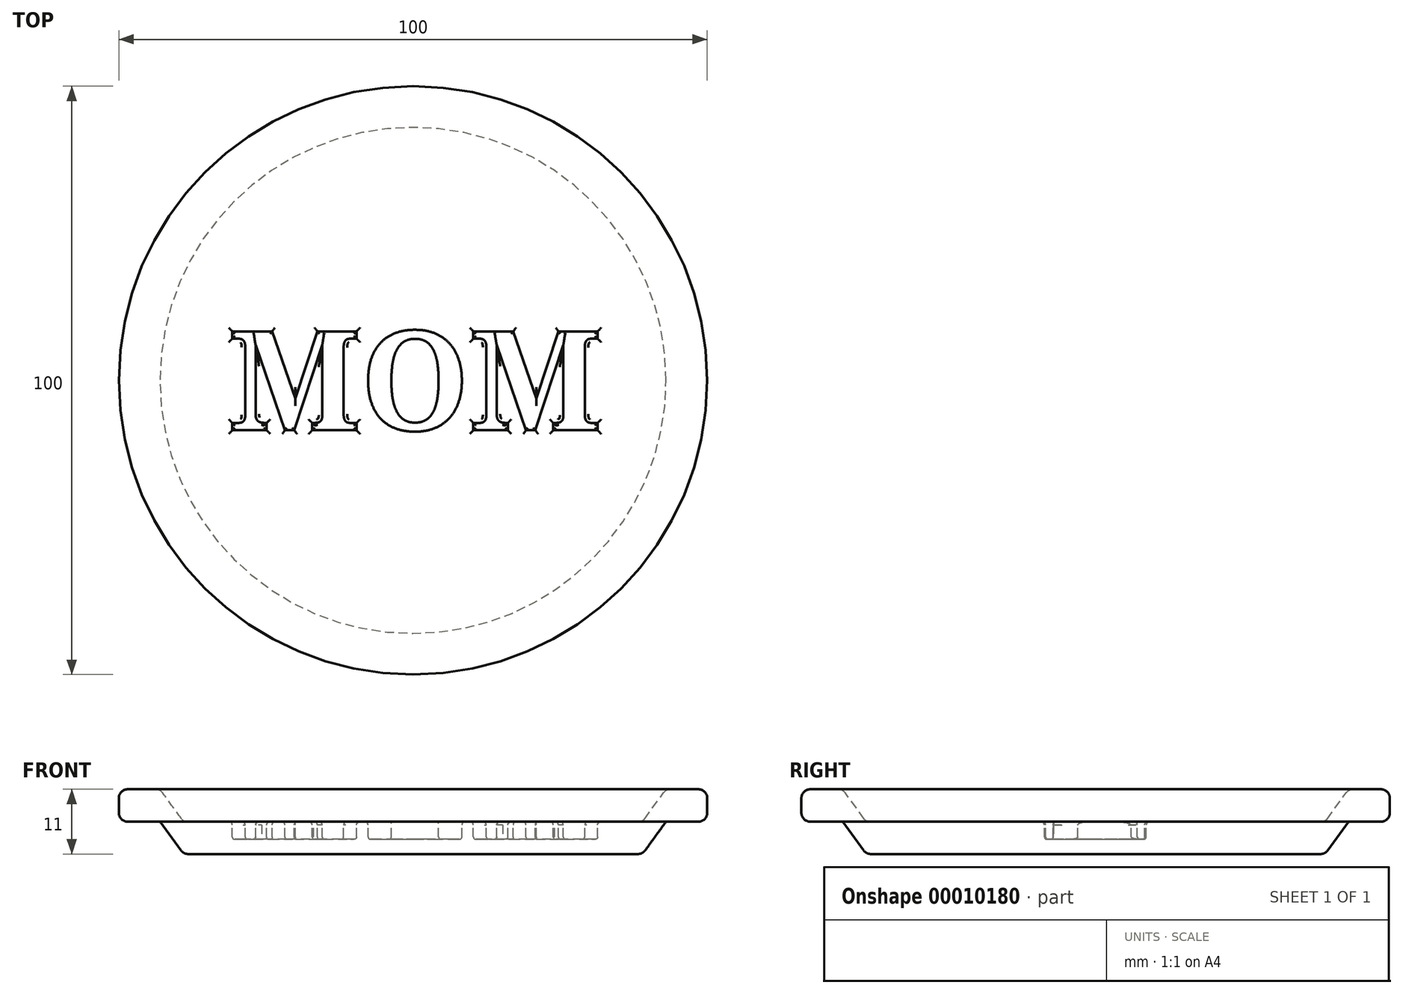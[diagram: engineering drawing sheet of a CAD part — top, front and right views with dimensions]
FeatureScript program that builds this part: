
annotation { "Feature Type Name" : "Feature", "Feature Type Description" : "" }
export const myFeature = defineFeature(function(context is Context, id is Id, definition is map)
    precondition{}
    {
        {
            var Q0;
            Q0=qCreatedBy(makeId("Front.planeOp"),FACE);
            var sketch = newSketch(context, id + "F0", { "sketchPlane" : qUnion([Q0])});
            skLineSegment(sketch, "E0", {"start": v(-39, 0) * mm, "end": v(0, 0) * mm});
            skLineSegment(sketch, "E1", {"start": v(-39, 0) * mm, "end": v(-43, 5.5) * mm});
            skLineSegment(sketch, "E2", {"start": v(-43, 5.5) * mm, "end": v(-50, 5.5) * mm});
            skLineSegment(sketch, "E3", {"start": v(-43, 0) * mm, "end": v(-39, 0) * mm, "construction": true});
            skLineSegment(sketch, "E4", {"start": v(-43, 0) * mm, "end": v(-43, 5.5) * mm, "construction": true});
            skLineSegment(sketch, "E5.0", {"start": v(-39, -5.5) * mm, "end": v(0, -5.5) * mm});
            skLineSegment(sketch, "E6.0", {"start": v(-43, 0) * mm, "end": v(-50, 0) * mm});
            skLineSegment(sketch, "E7", {"start": v(-43, 0) * mm, "end": v(-39, -5.5) * mm});
            skLineSegment(sketch, "E8", {"start": v(-50, 5.5) * mm, "end": v(-50, 0) * mm});
            skLineSegment(sketch, "E9", {"start": v(0, 0) * mm, "end": v(0, -5.5) * mm});
            skSolve(sketch);
        }
        {
            var Q0;
            Q0=qCreatedBy(makeId("Front.planeOp"),FACE);
            var sketch = newSketch(context, id + "F1", { "sketchPlane" : qUnion([Q0])});
            skLineSegment(sketch, "E10", {"start": v(0, 31.81) * mm, "end": v(0, -26.2) * mm});
            skSolve(sketch);
        }
        {
            var Q0;
            Q0=makeQuery(id+"F0.imprint","IMPRINT",FACE,{"disambiguationData":[TD([[makeQuery(id+"F0.imprint","IMPRINT",EDGE,{"derivedFrom":sQuery(id+"F0.wireOp",EDGE,"E0")}),-1.0]])]});
            var Q1;
            Q1=sQuery(id+"F1.wireOp",EDGE,"E10");
            revolve(context, id + "F2", {"entities" : qUnion([Q0]), "axis" : qUnion([Q1]), "revolveType" : RevolveType.FULL});
        }
        {
            var Q0;
            Q0=makeQuery(id+"F2.opRevolve","SWEPT_EDGE",EDGE,{"disambiguationData":[OSD([sQuery(id+"F0.wireOp",EDGE,"E1"),sQuery(id+"F0.wireOp",EDGE,"E2")])]});
            var Q1;
            Q1=makeQuery(id+"F2.opRevolve","SWEPT_EDGE",EDGE,{"disambiguationData":[OSD([sQuery(id+"F0.wireOp",EDGE,"E2"),sQuery(id+"F0.wireOp",EDGE,"E8")])]});
            var Q2;
            Q2=makeQuery(id+"F2.opRevolve","SWEPT_EDGE",EDGE,{"disambiguationData":[OSD([sQuery(id+"F0.wireOp",EDGE,"E6.0"),sQuery(id+"F0.wireOp",EDGE,"E8")])]});
            var Q3;
            Q3=makeQuery(id+"F2.opRevolve","SWEPT_EDGE",EDGE,{"disambiguationData":[OSD([sQuery(id+"F0.wireOp",EDGE,"E5.0"),sQuery(id+"F0.wireOp",EDGE,"E7")])]});
            fillet(context, id + "F3", {"entities" : qUnion([Q0, Q1, Q2, Q3]), "radius" : 1.5 * mm, "tangentPropagation" : true, "allowEdgeOverflow" : false});
        }
        {
            var Q0;
            Q0=makeQuery(id+"FGRXBjCafOSx1OX_1.boolean.opBoolean","COPY",EDGE,{"derivedFrom":makeQuery(id+"FGRXBjCafOSx1OX_1.opExtrude","CAP_EDGE",EDGE,{"disambiguationData":[OSD([sQuery(id+"FBqTZGQIcufDf44_1.wireOp",EDGE,"23bf69aa-c07b-4f37-bc8c-a48931fe9ff5.sketch_text.stroke-25")])],"isStart":true})});
            var Q1;
            Q1=makeQuery(id+"FGRXBjCafOSx1OX_1.boolean.opBoolean","COPY",EDGE,{"derivedFrom":makeQuery(id+"FGRXBjCafOSx1OX_1.opExtrude","CAP_EDGE",EDGE,{"disambiguationData":[OSD([sQuery(id+"FBqTZGQIcufDf44_1.wireOp",EDGE,"23bf69aa-c07b-4f37-bc8c-a48931fe9ff5.sketch_text.stroke-26")])],"isStart":true})});
            var Q2;
            Q2=makeQuery(id+"FGRXBjCafOSx1OX_1.boolean.opBoolean","SPLIT",FACE,{"disambiguationData":[TD([makeQuery(id+"F2.opRevolve","SWEPT_FACE",FACE,{"disambiguationData":[OSD([sQuery(id+"F0.wireOp",EDGE,"E1")])]})])],"derivedFrom":makeQuery(id+"F2.opRevolve","SWEPT_FACE",FACE,{"disambiguationData":[OSD([sQuery(id+"F0.wireOp",EDGE,"E0")])]})});
            var Q3;
            Q3=makeQuery(id+"FGRXBjCafOSx1OX_1.boolean.opBoolean","SPLIT",FACE,{"disambiguationData":[TD([makeQuery(id+"FGRXBjCafOSx1OX_1.opExtrude","SWEPT_FACE",FACE,{"disambiguationData":[OSD([sQuery(id+"FBqTZGQIcufDf44_1.wireOp",EDGE,"23bf69aa-c07b-4f37-bc8c-a48931fe9ff5.sketch_text.stroke-28")])]})])],"derivedFrom":makeQuery(id+"F2.opRevolve","SWEPT_FACE",FACE,{"disambiguationData":[OSD([sQuery(id+"F0.wireOp",EDGE,"E0")])]})});
            var Q4;
            Q4=makeQuery(id+"FGRXBjCafOSx1OX_1.boolean.opBoolean","SPLIT",FACE,{"disambiguationData":[TD([makeQuery(id+"FGRXBjCafOSx1OX_1.opExtrude","SWEPT_FACE",FACE,{"disambiguationData":[OSD([sQuery(id+"FBqTZGQIcufDf44_1.wireOp",EDGE,"23bf69aa-c07b-4f37-bc8c-a48931fe9ff5.sketch_text.stroke-39")])]})])],"derivedFrom":makeQuery(id+"F2.opRevolve","SWEPT_FACE",FACE,{"disambiguationData":[OSD([sQuery(id+"F0.wireOp",EDGE,"E0")])]})});
            var Q5;
            Q5=makeQuery(id+"FGRXBjCafOSx1OX_1.boolean.opBoolean","SPLIT",FACE,{"disambiguationData":[TD([makeQuery(id+"FGRXBjCafOSx1OX_1.opExtrude","SWEPT_FACE",FACE,{"disambiguationData":[OSD([sQuery(id+"FBqTZGQIcufDf44_1.wireOp",EDGE,"23bf69aa-c07b-4f37-bc8c-a48931fe9ff5.sketch_text.stroke-89")])]})])],"derivedFrom":makeQuery(id+"F2.opRevolve","SWEPT_FACE",FACE,{"disambiguationData":[OSD([sQuery(id+"F0.wireOp",EDGE,"E0")])]})});
            var Q6;
            Q6=makeQuery(id+"FGRXBjCafOSx1OX_1.boolean.opBoolean","SPLIT",FACE,{"disambiguationData":[TD([makeQuery(id+"FGRXBjCafOSx1OX_1.opExtrude","SWEPT_FACE",FACE,{"disambiguationData":[OSD([sQuery(id+"FBqTZGQIcufDf44_1.wireOp",EDGE,"23bf69aa-c07b-4f37-bc8c-a48931fe9ff5.sketch_text.stroke-78")])]})])],"derivedFrom":makeQuery(id+"F2.opRevolve","SWEPT_FACE",FACE,{"disambiguationData":[OSD([sQuery(id+"F0.wireOp",EDGE,"E0")])]})});
            var Q7;
            Q7=makeQuery(id+"FGRXBjCafOSx1OX_1.boolean.opBoolean","COPY",FACE,{"derivedFrom":makeQuery(id+"FGRXBjCafOSx1OX_1.opExtrude","CAP_FACE",FACE,{"disambiguationData":[OSD([sQuery(id+"FBqTZGQIcufDf44_1.wireOp",EDGE,"23bf69aa-c07b-4f37-bc8c-a48931fe9ff5.sketch_text.stroke-50"),sQuery(id+"FBqTZGQIcufDf44_1.wireOp",EDGE,"23bf69aa-c07b-4f37-bc8c-a48931fe9ff5.sketch_text.stroke-51"),sQuery(id+"FBqTZGQIcufDf44_1.wireOp",EDGE,"23bf69aa-c07b-4f37-bc8c-a48931fe9ff5.sketch_text.stroke-52"),sQuery(id+"FBqTZGQIcufDf44_1.wireOp",EDGE,"23bf69aa-c07b-4f37-bc8c-a48931fe9ff5.sketch_text.stroke-53"),sQuery(id+"FBqTZGQIcufDf44_1.wireOp",EDGE,"23bf69aa-c07b-4f37-bc8c-a48931fe9ff5.sketch_text.stroke-54"),sQuery(id+"FBqTZGQIcufDf44_1.wireOp",EDGE,"23bf69aa-c07b-4f37-bc8c-a48931fe9ff5.sketch_text.stroke-55"),sQuery(id+"FBqTZGQIcufDf44_1.wireOp",EDGE,"23bf69aa-c07b-4f37-bc8c-a48931fe9ff5.sketch_text.stroke-56"),sQuery(id+"FBqTZGQIcufDf44_1.wireOp",EDGE,"23bf69aa-c07b-4f37-bc8c-a48931fe9ff5.sketch_text.stroke-57"),sQuery(id+"FBqTZGQIcufDf44_1.wireOp",EDGE,"23bf69aa-c07b-4f37-bc8c-a48931fe9ff5.sketch_text.stroke-58"),sQuery(id+"FBqTZGQIcufDf44_1.wireOp",EDGE,"23bf69aa-c07b-4f37-bc8c-a48931fe9ff5.sketch_text.stroke-59"),sQuery(id+"FBqTZGQIcufDf44_1.wireOp",EDGE,"23bf69aa-c07b-4f37-bc8c-a48931fe9ff5.sketch_text.stroke-60"),sQuery(id+"FBqTZGQIcufDf44_1.wireOp",EDGE,"23bf69aa-c07b-4f37-bc8c-a48931fe9ff5.sketch_text.stroke-61"),sQuery(id+"FBqTZGQIcufDf44_1.wireOp",EDGE,"23bf69aa-c07b-4f37-bc8c-a48931fe9ff5.sketch_text.stroke-62"),sQuery(id+"FBqTZGQIcufDf44_1.wireOp",EDGE,"23bf69aa-c07b-4f37-bc8c-a48931fe9ff5.sketch_text.stroke-63"),sQuery(id+"FBqTZGQIcufDf44_1.wireOp",EDGE,"23bf69aa-c07b-4f37-bc8c-a48931fe9ff5.sketch_text.stroke-64"),sQuery(id+"FBqTZGQIcufDf44_1.wireOp",EDGE,"23bf69aa-c07b-4f37-bc8c-a48931fe9ff5.sketch_text.stroke-65"),sQuery(id+"FBqTZGQIcufDf44_1.wireOp",EDGE,"23bf69aa-c07b-4f37-bc8c-a48931fe9ff5.sketch_text.stroke-66"),sQuery(id+"FBqTZGQIcufDf44_1.wireOp",EDGE,"23bf69aa-c07b-4f37-bc8c-a48931fe9ff5.sketch_text.stroke-67"),sQuery(id+"FBqTZGQIcufDf44_1.wireOp",EDGE,"23bf69aa-c07b-4f37-bc8c-a48931fe9ff5.sketch_text.stroke-68"),sQuery(id+"FBqTZGQIcufDf44_1.wireOp",EDGE,"23bf69aa-c07b-4f37-bc8c-a48931fe9ff5.sketch_text.stroke-69"),sQuery(id+"FBqTZGQIcufDf44_1.wireOp",EDGE,"23bf69aa-c07b-4f37-bc8c-a48931fe9ff5.sketch_text.stroke-70"),sQuery(id+"FBqTZGQIcufDf44_1.wireOp",EDGE,"23bf69aa-c07b-4f37-bc8c-a48931fe9ff5.sketch_text.stroke-71"),sQuery(id+"FBqTZGQIcufDf44_1.wireOp",EDGE,"23bf69aa-c07b-4f37-bc8c-a48931fe9ff5.sketch_text.stroke-72"),sQuery(id+"FBqTZGQIcufDf44_1.wireOp",EDGE,"23bf69aa-c07b-4f37-bc8c-a48931fe9ff5.sketch_text.stroke-73"),sQuery(id+"FBqTZGQIcufDf44_1.wireOp",EDGE,"23bf69aa-c07b-4f37-bc8c-a48931fe9ff5.sketch_text.stroke-74"),sQuery(id+"FBqTZGQIcufDf44_1.wireOp",EDGE,"23bf69aa-c07b-4f37-bc8c-a48931fe9ff5.sketch_text.stroke-75"),sQuery(id+"FBqTZGQIcufDf44_1.wireOp",EDGE,"23bf69aa-c07b-4f37-bc8c-a48931fe9ff5.sketch_text.stroke-76"),sQuery(id+"FBqTZGQIcufDf44_1.wireOp",EDGE,"23bf69aa-c07b-4f37-bc8c-a48931fe9ff5.sketch_text.stroke-77"),sQuery(id+"FBqTZGQIcufDf44_1.wireOp",EDGE,"23bf69aa-c07b-4f37-bc8c-a48931fe9ff5.sketch_text.stroke-78"),sQuery(id+"FBqTZGQIcufDf44_1.wireOp",EDGE,"23bf69aa-c07b-4f37-bc8c-a48931fe9ff5.sketch_text.stroke-79"),sQuery(id+"FBqTZGQIcufDf44_1.wireOp",EDGE,"23bf69aa-c07b-4f37-bc8c-a48931fe9ff5.sketch_text.stroke-80"),sQuery(id+"FBqTZGQIcufDf44_1.wireOp",EDGE,"23bf69aa-c07b-4f37-bc8c-a48931fe9ff5.sketch_text.stroke-81"),sQuery(id+"FBqTZGQIcufDf44_1.wireOp",EDGE,"23bf69aa-c07b-4f37-bc8c-a48931fe9ff5.sketch_text.stroke-82"),sQuery(id+"FBqTZGQIcufDf44_1.wireOp",EDGE,"23bf69aa-c07b-4f37-bc8c-a48931fe9ff5.sketch_text.stroke-83"),sQuery(id+"FBqTZGQIcufDf44_1.wireOp",EDGE,"23bf69aa-c07b-4f37-bc8c-a48931fe9ff5.sketch_text.stroke-84"),sQuery(id+"FBqTZGQIcufDf44_1.wireOp",EDGE,"23bf69aa-c07b-4f37-bc8c-a48931fe9ff5.sketch_text.stroke-85"),sQuery(id+"FBqTZGQIcufDf44_1.wireOp",EDGE,"23bf69aa-c07b-4f37-bc8c-a48931fe9ff5.sketch_text.stroke-86"),sQuery(id+"FBqTZGQIcufDf44_1.wireOp",EDGE,"23bf69aa-c07b-4f37-bc8c-a48931fe9ff5.sketch_text.stroke-87"),sQuery(id+"FBqTZGQIcufDf44_1.wireOp",EDGE,"23bf69aa-c07b-4f37-bc8c-a48931fe9ff5.sketch_text.stroke-88"),sQuery(id+"FBqTZGQIcufDf44_1.wireOp",EDGE,"23bf69aa-c07b-4f37-bc8c-a48931fe9ff5.sketch_text.stroke-89"),sQuery(id+"FBqTZGQIcufDf44_1.wireOp",EDGE,"23bf69aa-c07b-4f37-bc8c-a48931fe9ff5.sketch_text.stroke-90"),sQuery(id+"FBqTZGQIcufDf44_1.wireOp",EDGE,"23bf69aa-c07b-4f37-bc8c-a48931fe9ff5.sketch_text.stroke-91"),sQuery(id+"FBqTZGQIcufDf44_1.wireOp",EDGE,"23bf69aa-c07b-4f37-bc8c-a48931fe9ff5.sketch_text.stroke-92"),sQuery(id+"FBqTZGQIcufDf44_1.wireOp",EDGE,"23bf69aa-c07b-4f37-bc8c-a48931fe9ff5.sketch_text.stroke-93"),sQuery(id+"FBqTZGQIcufDf44_1.wireOp",EDGE,"23bf69aa-c07b-4f37-bc8c-a48931fe9ff5.sketch_text.stroke-94"),sQuery(id+"FBqTZGQIcufDf44_1.wireOp",EDGE,"23bf69aa-c07b-4f37-bc8c-a48931fe9ff5.sketch_text.stroke-95"),sQuery(id+"FBqTZGQIcufDf44_1.wireOp",EDGE,"23bf69aa-c07b-4f37-bc8c-a48931fe9ff5.sketch_text.stroke-96"),sQuery(id+"FBqTZGQIcufDf44_1.wireOp",EDGE,"23bf69aa-c07b-4f37-bc8c-a48931fe9ff5.sketch_text.stroke-97"),sQuery(id+"FBqTZGQIcufDf44_1.wireOp",EDGE,"23bf69aa-c07b-4f37-bc8c-a48931fe9ff5.sketch_text.stroke-98"),sQuery(id+"FBqTZGQIcufDf44_1.wireOp",EDGE,"23bf69aa-c07b-4f37-bc8c-a48931fe9ff5.sketch_text.stroke-99")])],"isStart":false})});
            var Q8;
            Q8=makeQuery(id+"FGRXBjCafOSx1OX_1.boolean.opBoolean","COPY",FACE,{"derivedFrom":makeQuery(id+"FGRXBjCafOSx1OX_1.opExtrude","CAP_FACE",FACE,{"disambiguationData":[OSD([sQuery(id+"FBqTZGQIcufDf44_1.wireOp",EDGE,"23bf69aa-c07b-4f37-bc8c-a48931fe9ff5.sketch_text.stroke-0"),sQuery(id+"FBqTZGQIcufDf44_1.wireOp",EDGE,"23bf69aa-c07b-4f37-bc8c-a48931fe9ff5.sketch_text.stroke-1"),sQuery(id+"FBqTZGQIcufDf44_1.wireOp",EDGE,"23bf69aa-c07b-4f37-bc8c-a48931fe9ff5.sketch_text.stroke-2"),sQuery(id+"FBqTZGQIcufDf44_1.wireOp",EDGE,"23bf69aa-c07b-4f37-bc8c-a48931fe9ff5.sketch_text.stroke-3"),sQuery(id+"FBqTZGQIcufDf44_1.wireOp",EDGE,"23bf69aa-c07b-4f37-bc8c-a48931fe9ff5.sketch_text.stroke-4"),sQuery(id+"FBqTZGQIcufDf44_1.wireOp",EDGE,"23bf69aa-c07b-4f37-bc8c-a48931fe9ff5.sketch_text.stroke-5"),sQuery(id+"FBqTZGQIcufDf44_1.wireOp",EDGE,"23bf69aa-c07b-4f37-bc8c-a48931fe9ff5.sketch_text.stroke-6"),sQuery(id+"FBqTZGQIcufDf44_1.wireOp",EDGE,"23bf69aa-c07b-4f37-bc8c-a48931fe9ff5.sketch_text.stroke-7"),sQuery(id+"FBqTZGQIcufDf44_1.wireOp",EDGE,"23bf69aa-c07b-4f37-bc8c-a48931fe9ff5.sketch_text.stroke-8"),sQuery(id+"FBqTZGQIcufDf44_1.wireOp",EDGE,"23bf69aa-c07b-4f37-bc8c-a48931fe9ff5.sketch_text.stroke-9"),sQuery(id+"FBqTZGQIcufDf44_1.wireOp",EDGE,"23bf69aa-c07b-4f37-bc8c-a48931fe9ff5.sketch_text.stroke-10"),sQuery(id+"FBqTZGQIcufDf44_1.wireOp",EDGE,"23bf69aa-c07b-4f37-bc8c-a48931fe9ff5.sketch_text.stroke-11"),sQuery(id+"FBqTZGQIcufDf44_1.wireOp",EDGE,"23bf69aa-c07b-4f37-bc8c-a48931fe9ff5.sketch_text.stroke-12"),sQuery(id+"FBqTZGQIcufDf44_1.wireOp",EDGE,"23bf69aa-c07b-4f37-bc8c-a48931fe9ff5.sketch_text.stroke-13"),sQuery(id+"FBqTZGQIcufDf44_1.wireOp",EDGE,"23bf69aa-c07b-4f37-bc8c-a48931fe9ff5.sketch_text.stroke-14"),sQuery(id+"FBqTZGQIcufDf44_1.wireOp",EDGE,"23bf69aa-c07b-4f37-bc8c-a48931fe9ff5.sketch_text.stroke-15"),sQuery(id+"FBqTZGQIcufDf44_1.wireOp",EDGE,"23bf69aa-c07b-4f37-bc8c-a48931fe9ff5.sketch_text.stroke-16"),sQuery(id+"FBqTZGQIcufDf44_1.wireOp",EDGE,"23bf69aa-c07b-4f37-bc8c-a48931fe9ff5.sketch_text.stroke-17"),sQuery(id+"FBqTZGQIcufDf44_1.wireOp",EDGE,"23bf69aa-c07b-4f37-bc8c-a48931fe9ff5.sketch_text.stroke-18"),sQuery(id+"FBqTZGQIcufDf44_1.wireOp",EDGE,"23bf69aa-c07b-4f37-bc8c-a48931fe9ff5.sketch_text.stroke-19"),sQuery(id+"FBqTZGQIcufDf44_1.wireOp",EDGE,"23bf69aa-c07b-4f37-bc8c-a48931fe9ff5.sketch_text.stroke-20"),sQuery(id+"FBqTZGQIcufDf44_1.wireOp",EDGE,"23bf69aa-c07b-4f37-bc8c-a48931fe9ff5.sketch_text.stroke-21"),sQuery(id+"FBqTZGQIcufDf44_1.wireOp",EDGE,"23bf69aa-c07b-4f37-bc8c-a48931fe9ff5.sketch_text.stroke-22"),sQuery(id+"FBqTZGQIcufDf44_1.wireOp",EDGE,"23bf69aa-c07b-4f37-bc8c-a48931fe9ff5.sketch_text.stroke-23"),sQuery(id+"FBqTZGQIcufDf44_1.wireOp",EDGE,"23bf69aa-c07b-4f37-bc8c-a48931fe9ff5.sketch_text.stroke-24"),sQuery(id+"FBqTZGQIcufDf44_1.wireOp",EDGE,"23bf69aa-c07b-4f37-bc8c-a48931fe9ff5.sketch_text.stroke-25"),sQuery(id+"FBqTZGQIcufDf44_1.wireOp",EDGE,"23bf69aa-c07b-4f37-bc8c-a48931fe9ff5.sketch_text.stroke-26"),sQuery(id+"FBqTZGQIcufDf44_1.wireOp",EDGE,"23bf69aa-c07b-4f37-bc8c-a48931fe9ff5.sketch_text.stroke-27"),sQuery(id+"FBqTZGQIcufDf44_1.wireOp",EDGE,"23bf69aa-c07b-4f37-bc8c-a48931fe9ff5.sketch_text.stroke-28"),sQuery(id+"FBqTZGQIcufDf44_1.wireOp",EDGE,"23bf69aa-c07b-4f37-bc8c-a48931fe9ff5.sketch_text.stroke-29"),sQuery(id+"FBqTZGQIcufDf44_1.wireOp",EDGE,"23bf69aa-c07b-4f37-bc8c-a48931fe9ff5.sketch_text.stroke-30"),sQuery(id+"FBqTZGQIcufDf44_1.wireOp",EDGE,"23bf69aa-c07b-4f37-bc8c-a48931fe9ff5.sketch_text.stroke-31"),sQuery(id+"FBqTZGQIcufDf44_1.wireOp",EDGE,"23bf69aa-c07b-4f37-bc8c-a48931fe9ff5.sketch_text.stroke-32"),sQuery(id+"FBqTZGQIcufDf44_1.wireOp",EDGE,"23bf69aa-c07b-4f37-bc8c-a48931fe9ff5.sketch_text.stroke-33"),sQuery(id+"FBqTZGQIcufDf44_1.wireOp",EDGE,"23bf69aa-c07b-4f37-bc8c-a48931fe9ff5.sketch_text.stroke-34"),sQuery(id+"FBqTZGQIcufDf44_1.wireOp",EDGE,"23bf69aa-c07b-4f37-bc8c-a48931fe9ff5.sketch_text.stroke-35"),sQuery(id+"FBqTZGQIcufDf44_1.wireOp",EDGE,"23bf69aa-c07b-4f37-bc8c-a48931fe9ff5.sketch_text.stroke-36"),sQuery(id+"FBqTZGQIcufDf44_1.wireOp",EDGE,"23bf69aa-c07b-4f37-bc8c-a48931fe9ff5.sketch_text.stroke-37"),sQuery(id+"FBqTZGQIcufDf44_1.wireOp",EDGE,"23bf69aa-c07b-4f37-bc8c-a48931fe9ff5.sketch_text.stroke-38"),sQuery(id+"FBqTZGQIcufDf44_1.wireOp",EDGE,"23bf69aa-c07b-4f37-bc8c-a48931fe9ff5.sketch_text.stroke-39"),sQuery(id+"FBqTZGQIcufDf44_1.wireOp",EDGE,"23bf69aa-c07b-4f37-bc8c-a48931fe9ff5.sketch_text.stroke-40"),sQuery(id+"FBqTZGQIcufDf44_1.wireOp",EDGE,"23bf69aa-c07b-4f37-bc8c-a48931fe9ff5.sketch_text.stroke-41"),sQuery(id+"FBqTZGQIcufDf44_1.wireOp",EDGE,"23bf69aa-c07b-4f37-bc8c-a48931fe9ff5.sketch_text.stroke-42"),sQuery(id+"FBqTZGQIcufDf44_1.wireOp",EDGE,"23bf69aa-c07b-4f37-bc8c-a48931fe9ff5.sketch_text.stroke-43"),sQuery(id+"FBqTZGQIcufDf44_1.wireOp",EDGE,"23bf69aa-c07b-4f37-bc8c-a48931fe9ff5.sketch_text.stroke-44"),sQuery(id+"FBqTZGQIcufDf44_1.wireOp",EDGE,"23bf69aa-c07b-4f37-bc8c-a48931fe9ff5.sketch_text.stroke-45"),sQuery(id+"FBqTZGQIcufDf44_1.wireOp",EDGE,"23bf69aa-c07b-4f37-bc8c-a48931fe9ff5.sketch_text.stroke-46"),sQuery(id+"FBqTZGQIcufDf44_1.wireOp",EDGE,"23bf69aa-c07b-4f37-bc8c-a48931fe9ff5.sketch_text.stroke-47"),sQuery(id+"FBqTZGQIcufDf44_1.wireOp",EDGE,"23bf69aa-c07b-4f37-bc8c-a48931fe9ff5.sketch_text.stroke-48"),sQuery(id+"FBqTZGQIcufDf44_1.wireOp",EDGE,"23bf69aa-c07b-4f37-bc8c-a48931fe9ff5.sketch_text.stroke-49")])],"isStart":false})});
            fillet(context, id + "F4", {"entities" : qUnion([Q0, Q1, Q2, Q3, Q4, Q5, Q6, Q7, Q8]), "radius" : 1 * mm, "tangentPropagation" : true, "allowEdgeOverflow" : false});
        }
        {
            var Q0;
            Q0=qCreatedBy(makeId("Top.planeOp"),FACE);
            var sketch = newSketch(context, id + "F5", { "sketchPlane" : qUnion([Q0])});
            skText(sketch, "E11", { "text": "MOM", "fontName": "NotoSerif-Bold.ttf"});
            skCircle(sketch, "E12", {"center": v(0, 0) * mm, "radius": 32.5 * mm, "construction": true});
            const initialGuessF5  = {"E11": [-0.03137, -0.00848, 1, 0, 0.01696]};
            skSetInitialGuess(sketch, initialGuessF5);
            skSolve(sketch);
        }
        {
            var Q0;
            Q0 = qSketchRegion(id + "F5", true);
            extrude(context, id + "F6", {"entities" : qUnion([Q0]), "operationType" : NewBodyOperationType.REMOVE, "oppositeDirection" : true, "depth" : 3 * mm});
        }
        {
            var Q0;
            Q0=makeQuery(id+"F6.boolean.opBoolean","COPY",EDGE,{"derivedFrom":makeQuery(id+"F6.opExtrude","CAP_EDGE",EDGE,{"disambiguationData":[OSD([sQuery(id+"F5.wireOp",EDGE,"E11.sketch_text.stroke-31")])],"isStart":true})});
            var Q1;
            Q1=makeQuery(id+"F6.boolean.opBoolean","COPY",EDGE,{"derivedFrom":makeQuery(id+"F6.opExtrude","CAP_EDGE",EDGE,{"disambiguationData":[OSD([sQuery(id+"F5.wireOp",EDGE,"E11.sketch_text.stroke-32")])],"isStart":true})});
            var Q2;
            Q2=makeQuery(id+"F6.boolean.opBoolean","COPY",EDGE,{"derivedFrom":makeQuery(id+"F6.opExtrude","CAP_EDGE",EDGE,{"disambiguationData":[OSD([sQuery(id+"F5.wireOp",EDGE,"E11.sketch_text.stroke-33")])],"isStart":true})});
            var Q3;
            Q3=makeQuery(id+"F6.boolean.opBoolean","COPY",EDGE,{"derivedFrom":makeQuery(id+"F6.opExtrude","CAP_EDGE",EDGE,{"disambiguationData":[OSD([sQuery(id+"F5.wireOp",EDGE,"E11.sketch_text.stroke-34")])],"isStart":true})});
            var Q4;
            Q4=makeQuery(id+"F6.boolean.opBoolean","COPY",EDGE,{"derivedFrom":makeQuery(id+"F6.opExtrude","CAP_EDGE",EDGE,{"disambiguationData":[OSD([sQuery(id+"F5.wireOp",EDGE,"E11.sketch_text.stroke-6")])],"isStart":true})});
            var Q5;
            Q5=makeQuery(id+"F6.boolean.opBoolean","COPY",EDGE,{"derivedFrom":makeQuery(id+"F6.opExtrude","CAP_EDGE",EDGE,{"disambiguationData":[OSD([sQuery(id+"F5.wireOp",EDGE,"E11.sketch_text.stroke-7")])],"isStart":true})});
            var Q6;
            Q6=makeQuery(id+"F6.boolean.opBoolean","COPY",EDGE,{"derivedFrom":makeQuery(id+"F6.opExtrude","CAP_EDGE",EDGE,{"disambiguationData":[OSD([sQuery(id+"F5.wireOp",EDGE,"E11.sketch_text.stroke-41")])],"isStart":true})});
            var Q7;
            Q7=makeQuery(id+"F6.boolean.opBoolean","COPY",EDGE,{"derivedFrom":makeQuery(id+"F6.opExtrude","CAP_EDGE",EDGE,{"disambiguationData":[OSD([sQuery(id+"F5.wireOp",EDGE,"E11.sketch_text.stroke-36")])],"isStart":true})});
            var Q8;
            Q8=makeQuery(id+"F6.boolean.opBoolean","COPY",EDGE,{"derivedFrom":makeQuery(id+"F6.opExtrude","CAP_EDGE",EDGE,{"disambiguationData":[OSD([sQuery(id+"F5.wireOp",EDGE,"E11.sketch_text.stroke-46")])],"isStart":true})});
            var Q9;
            Q9=makeQuery(id+"F6.boolean.opBoolean","COPY",EDGE,{"derivedFrom":makeQuery(id+"F6.opExtrude","CAP_EDGE",EDGE,{"disambiguationData":[OSD([sQuery(id+"F5.wireOp",EDGE,"E11.sketch_text.stroke-48")])],"isStart":true})});
            var Q10;
            Q10=makeQuery(id+"F6.boolean.opBoolean","COPY",EDGE,{"derivedFrom":makeQuery(id+"F6.opExtrude","CAP_EDGE",EDGE,{"disambiguationData":[OSD([sQuery(id+"F5.wireOp",EDGE,"E11.sketch_text.stroke-9")])],"isStart":true})});
            var Q11;
            Q11=makeQuery(id+"F6.boolean.opBoolean","COPY",EDGE,{"derivedFrom":makeQuery(id+"F6.opExtrude","CAP_EDGE",EDGE,{"disambiguationData":[OSD([sQuery(id+"F5.wireOp",EDGE,"E11.sketch_text.stroke-10")])],"isStart":true})});
            var Q12;
            Q12=makeQuery(id+"F6.boolean.opBoolean","COPY",EDGE,{"derivedFrom":makeQuery(id+"F6.opExtrude","CAP_EDGE",EDGE,{"disambiguationData":[OSD([sQuery(id+"F5.wireOp",EDGE,"E11.sketch_text.stroke-24")])],"isStart":true})});
            var Q13;
            Q13=makeQuery(id+"F6.boolean.opBoolean","COPY",EDGE,{"derivedFrom":makeQuery(id+"F6.opExtrude","CAP_EDGE",EDGE,{"disambiguationData":[OSD([sQuery(id+"F5.wireOp",EDGE,"E11.sketch_text.stroke-30")])],"isStart":true})});
            var Q14;
            Q14=makeQuery(id+"F6.boolean.opBoolean","COPY",EDGE,{"derivedFrom":makeQuery(id+"F6.opExtrude","CAP_EDGE",EDGE,{"disambiguationData":[OSD([sQuery(id+"F5.wireOp",EDGE,"E11.sketch_text.stroke-29")])],"isStart":true})});
            var Q15;
            Q15=makeQuery(id+"F6.boolean.opBoolean","COPY",EDGE,{"derivedFrom":makeQuery(id+"F6.opExtrude","CAP_EDGE",EDGE,{"disambiguationData":[OSD([sQuery(id+"F5.wireOp",EDGE,"E11.sketch_text.stroke-35")])],"isStart":true})});
            var Q16;
            Q16=makeQuery(id+"F6.boolean.opBoolean","COPY",EDGE,{"derivedFrom":makeQuery(id+"F6.opExtrude","CAP_EDGE",EDGE,{"disambiguationData":[OSD([sQuery(id+"F5.wireOp",EDGE,"E11.sketch_text.stroke-17")])],"isStart":true})});
            var Q17;
            Q17=makeQuery(id+"F6.boolean.opBoolean","COPY",EDGE,{"derivedFrom":makeQuery(id+"F6.opExtrude","CAP_EDGE",EDGE,{"disambiguationData":[OSD([sQuery(id+"F5.wireOp",EDGE,"E11.sketch_text.stroke-18")])],"isStart":true})});
            var Q18;
            Q18=makeQuery(id+"F6.boolean.opBoolean","COPY",EDGE,{"derivedFrom":makeQuery(id+"F6.opExtrude","CAP_EDGE",EDGE,{"disambiguationData":[OSD([sQuery(id+"F5.wireOp",EDGE,"E11.sketch_text.stroke-19")])],"isStart":true})});
            var Q19;
            Q19=makeQuery(id+"F6.boolean.opBoolean","COPY",EDGE,{"derivedFrom":makeQuery(id+"F6.opExtrude","CAP_EDGE",EDGE,{"disambiguationData":[OSD([sQuery(id+"F5.wireOp",EDGE,"E11.sketch_text.stroke-16")])],"isStart":true})});
            var Q20;
            Q20=makeQuery(id+"F6.boolean.opBoolean","COPY",EDGE,{"derivedFrom":makeQuery(id+"F6.opExtrude","CAP_EDGE",EDGE,{"disambiguationData":[OSD([sQuery(id+"F5.wireOp",EDGE,"E11.sketch_text.stroke-11")])],"isStart":true})});
            var Q21;
            Q21=makeQuery(id+"F6.boolean.opBoolean","COPY",EDGE,{"derivedFrom":makeQuery(id+"F6.opExtrude","CAP_EDGE",EDGE,{"disambiguationData":[OSD([sQuery(id+"F5.wireOp",EDGE,"E11.sketch_text.stroke-1")])],"isStart":true})});
            var Q22;
            Q22=makeQuery(id+"F6.boolean.opBoolean","COPY",EDGE,{"derivedFrom":makeQuery(id+"F6.opExtrude","CAP_EDGE",EDGE,{"disambiguationData":[OSD([sQuery(id+"F5.wireOp",EDGE,"E11.sketch_text.stroke-15")])],"isStart":true})});
            var Q23;
            Q23=makeQuery(id+"F6.boolean.opBoolean","COPY",EDGE,{"derivedFrom":makeQuery(id+"F6.opExtrude","CAP_EDGE",EDGE,{"disambiguationData":[OSD([sQuery(id+"F5.wireOp",EDGE,"E11.sketch_text.stroke-0")])],"isStart":true})});
            var Q24;
            Q24=makeQuery(id+"F6.boolean.opBoolean","COPY",EDGE,{"derivedFrom":makeQuery(id+"F6.opExtrude","CAP_EDGE",EDGE,{"disambiguationData":[OSD([sQuery(id+"F5.wireOp",EDGE,"E11.sketch_text.stroke-47")])],"isStart":true})});
            var Q25;
            Q25=makeQuery(id+"F6.boolean.opBoolean","COPY",EDGE,{"derivedFrom":makeQuery(id+"F6.opExtrude","CAP_EDGE",EDGE,{"disambiguationData":[OSD([sQuery(id+"F5.wireOp",EDGE,"E11.sketch_text.stroke-8")])],"isStart":true})});
            fillet(context, id + "F7", {"entities" : qUnion([Q0, Q1, Q2, Q3, Q4, Q5, Q6, Q7, Q8, Q9, Q10, Q11, Q12, Q13, Q14, Q15, Q16, Q17, Q18, Q19, Q20, Q21, Q22, Q23, Q24, Q25]), "radius" : 0.6 * mm, "allowEdgeOverflow" : false});
        }
        {
            var Q0;
            Q0=makeQuery(id+"F6.boolean.opBoolean","COPY",EDGE,{"derivedFrom":makeQuery(id+"F6.opExtrude","CAP_EDGE",EDGE,{"disambiguationData":[OSD([sQuery(id+"F5.wireOp",EDGE,"E11.sketch_text.stroke-80")])],"isStart":true})});
            var Q1;
            Q1=makeQuery(id+"F6.boolean.opBoolean","COPY",EDGE,{"derivedFrom":makeQuery(id+"F6.opExtrude","CAP_EDGE",EDGE,{"disambiguationData":[OSD([sQuery(id+"F5.wireOp",EDGE,"E11.sketch_text.stroke-57")])],"isStart":true})});
            fillet(context, id + "F8", {"entities" : qUnion([Q0, Q1]), "radius" : 0.6 * mm, "tangentPropagation" : true, "allowEdgeOverflow" : false});
        }
        {
            var Q0;
            Q0=makeQuery(id+"F6.boolean.opBoolean","COPY",EDGE,{"derivedFrom":makeQuery(id+"F6.opExtrude","CAP_EDGE",EDGE,{"disambiguationData":[OSD([sQuery(id+"F5.wireOp",EDGE,"E11.sketch_text.stroke-105")])],"isStart":true})});
            var Q1;
            Q1=makeQuery(id+"F6.boolean.opBoolean","COPY",EDGE,{"derivedFrom":makeQuery(id+"F6.opExtrude","CAP_EDGE",EDGE,{"disambiguationData":[OSD([sQuery(id+"F5.wireOp",EDGE,"E11.sketch_text.stroke-91")])],"isStart":true})});
            var Q2;
            Q2=makeQuery(id+"F6.boolean.opBoolean","COPY",EDGE,{"derivedFrom":makeQuery(id+"F6.opExtrude","CAP_EDGE",EDGE,{"disambiguationData":[OSD([sQuery(id+"F5.wireOp",EDGE,"E11.sketch_text.stroke-90")])],"isStart":true})});
            var Q3;
            Q3=makeQuery(id+"F6.boolean.opBoolean","COPY",EDGE,{"derivedFrom":makeQuery(id+"F6.opExtrude","CAP_EDGE",EDGE,{"disambiguationData":[OSD([sQuery(id+"F5.wireOp",EDGE,"E11.sketch_text.stroke-89")])],"isStart":true})});
            var Q4;
            Q4=makeQuery(id+"F6.boolean.opBoolean","COPY",EDGE,{"derivedFrom":makeQuery(id+"F6.opExtrude","CAP_EDGE",EDGE,{"disambiguationData":[OSD([sQuery(id+"F5.wireOp",EDGE,"E11.sketch_text.stroke-88")])],"isStart":true})});
            var Q5;
            Q5=makeQuery(id+"F6.boolean.opBoolean","COPY",EDGE,{"derivedFrom":makeQuery(id+"F6.opExtrude","CAP_EDGE",EDGE,{"disambiguationData":[OSD([sQuery(id+"F5.wireOp",EDGE,"E11.sketch_text.stroke-87")])],"isStart":true})});
            var Q6;
            Q6=makeQuery(id+"F6.boolean.opBoolean","COPY",EDGE,{"derivedFrom":makeQuery(id+"F6.opExtrude","CAP_EDGE",EDGE,{"disambiguationData":[OSD([sQuery(id+"F5.wireOp",EDGE,"E11.sketch_text.stroke-129")])],"isStart":true})});
            var Q7;
            Q7=makeQuery(id+"F6.boolean.opBoolean","COPY",EDGE,{"derivedFrom":makeQuery(id+"F6.opExtrude","CAP_EDGE",EDGE,{"disambiguationData":[OSD([sQuery(id+"F5.wireOp",EDGE,"E11.sketch_text.stroke-122")])],"isStart":true})});
            var Q8;
            Q8=makeQuery(id+"F6.boolean.opBoolean","COPY",EDGE,{"derivedFrom":makeQuery(id+"F6.opExtrude","CAP_EDGE",EDGE,{"disambiguationData":[OSD([sQuery(id+"F5.wireOp",EDGE,"E11.sketch_text.stroke-112")])],"isStart":true})});
            var Q9;
            Q9=makeQuery(id+"F6.boolean.opBoolean","COPY",EDGE,{"derivedFrom":makeQuery(id+"F6.opExtrude","CAP_EDGE",EDGE,{"disambiguationData":[OSD([sQuery(id+"F5.wireOp",EDGE,"E11.sketch_text.stroke-113")])],"isStart":true})});
            var Q10;
            Q10=makeQuery(id+"F6.boolean.opBoolean","COPY",EDGE,{"derivedFrom":makeQuery(id+"F6.opExtrude","CAP_EDGE",EDGE,{"disambiguationData":[OSD([sQuery(id+"F5.wireOp",EDGE,"E11.sketch_text.stroke-114")])],"isStart":true})});
            var Q11;
            Q11=makeQuery(id+"F6.boolean.opBoolean","COPY",EDGE,{"derivedFrom":makeQuery(id+"F6.opExtrude","CAP_EDGE",EDGE,{"disambiguationData":[OSD([sQuery(id+"F5.wireOp",EDGE,"E11.sketch_text.stroke-115")])],"isStart":true})});
            var Q12;
            Q12=makeQuery(id+"F6.boolean.opBoolean","COPY",EDGE,{"derivedFrom":makeQuery(id+"F6.opExtrude","CAP_EDGE",EDGE,{"disambiguationData":[OSD([sQuery(id+"F5.wireOp",EDGE,"E11.sketch_text.stroke-111")])],"isStart":true})});
            var Q13;
            Q13=makeQuery(id+"F6.boolean.opBoolean","COPY",EDGE,{"derivedFrom":makeQuery(id+"F6.opExtrude","CAP_EDGE",EDGE,{"disambiguationData":[OSD([sQuery(id+"F5.wireOp",EDGE,"E11.sketch_text.stroke-116")])],"isStart":true})});
            var Q14;
            Q14=makeQuery(id+"F6.boolean.opBoolean","COPY",EDGE,{"derivedFrom":makeQuery(id+"F6.opExtrude","CAP_EDGE",EDGE,{"disambiguationData":[OSD([sQuery(id+"F5.wireOp",EDGE,"E11.sketch_text.stroke-128")])],"isStart":true})});
            var Q15;
            Q15=makeQuery(id+"F6.boolean.opBoolean","COPY",EDGE,{"derivedFrom":makeQuery(id+"F6.opExtrude","CAP_EDGE",EDGE,{"disambiguationData":[OSD([sQuery(id+"F5.wireOp",EDGE,"E11.sketch_text.stroke-81")])],"isStart":true})});
            var Q16;
            Q16=makeQuery(id+"F6.boolean.opBoolean","COPY",EDGE,{"derivedFrom":makeQuery(id+"F6.opExtrude","CAP_EDGE",EDGE,{"disambiguationData":[OSD([sQuery(id+"F5.wireOp",EDGE,"E11.sketch_text.stroke-97")])],"isStart":true})});
            var Q17;
            Q17=makeQuery(id+"F6.boolean.opBoolean","COPY",EDGE,{"derivedFrom":makeQuery(id+"F6.opExtrude","CAP_EDGE",EDGE,{"disambiguationData":[OSD([sQuery(id+"F5.wireOp",EDGE,"E11.sketch_text.stroke-98")])],"isStart":true})});
            var Q18;
            Q18=makeQuery(id+"F6.boolean.opBoolean","COPY",EDGE,{"derivedFrom":makeQuery(id+"F6.opExtrude","CAP_EDGE",EDGE,{"disambiguationData":[OSD([sQuery(id+"F5.wireOp",EDGE,"E11.sketch_text.stroke-99")])],"isStart":true})});
            fillet(context, id + "F9", {"entities" : qUnion([Q0, Q1, Q2, Q3, Q4, Q5, Q6, Q7, Q8, Q9, Q10, Q11, Q12, Q13, Q14, Q15, Q16, Q17, Q18]), "radius" : 0.6 * mm, "tangentPropagation" : true, "allowEdgeOverflow" : false});
        }
        {
            var Q0;
            Q0=makeQuery(id+"F6.boolean.opBoolean","COPY",FACE,{"derivedFrom":makeQuery(id+"F6.opExtrude","CAP_FACE",FACE,{"disambiguationData":[OSD([sQuery(id+"F5.wireOp",EDGE,"E11.sketch_text.stroke-0"),sQuery(id+"F5.wireOp",EDGE,"E11.sketch_text.stroke-1"),sQuery(id+"F5.wireOp",EDGE,"E11.sketch_text.stroke-2"),sQuery(id+"F5.wireOp",EDGE,"E11.sketch_text.stroke-3"),sQuery(id+"F5.wireOp",EDGE,"E11.sketch_text.stroke-4"),sQuery(id+"F5.wireOp",EDGE,"E11.sketch_text.stroke-5"),sQuery(id+"F5.wireOp",EDGE,"E11.sketch_text.stroke-6"),sQuery(id+"F5.wireOp",EDGE,"E11.sketch_text.stroke-7"),sQuery(id+"F5.wireOp",EDGE,"E11.sketch_text.stroke-8"),sQuery(id+"F5.wireOp",EDGE,"E11.sketch_text.stroke-9"),sQuery(id+"F5.wireOp",EDGE,"E11.sketch_text.stroke-10"),sQuery(id+"F5.wireOp",EDGE,"E11.sketch_text.stroke-11"),sQuery(id+"F5.wireOp",EDGE,"E11.sketch_text.stroke-12"),sQuery(id+"F5.wireOp",EDGE,"E11.sketch_text.stroke-13"),sQuery(id+"F5.wireOp",EDGE,"E11.sketch_text.stroke-14"),sQuery(id+"F5.wireOp",EDGE,"E11.sketch_text.stroke-15"),sQuery(id+"F5.wireOp",EDGE,"E11.sketch_text.stroke-16"),sQuery(id+"F5.wireOp",EDGE,"E11.sketch_text.stroke-17"),sQuery(id+"F5.wireOp",EDGE,"E11.sketch_text.stroke-18"),sQuery(id+"F5.wireOp",EDGE,"E11.sketch_text.stroke-19"),sQuery(id+"F5.wireOp",EDGE,"E11.sketch_text.stroke-20"),sQuery(id+"F5.wireOp",EDGE,"E11.sketch_text.stroke-21"),sQuery(id+"F5.wireOp",EDGE,"E11.sketch_text.stroke-22"),sQuery(id+"F5.wireOp",EDGE,"E11.sketch_text.stroke-23"),sQuery(id+"F5.wireOp",EDGE,"E11.sketch_text.stroke-24"),sQuery(id+"F5.wireOp",EDGE,"E11.sketch_text.stroke-25"),sQuery(id+"F5.wireOp",EDGE,"E11.sketch_text.stroke-26"),sQuery(id+"F5.wireOp",EDGE,"E11.sketch_text.stroke-27"),sQuery(id+"F5.wireOp",EDGE,"E11.sketch_text.stroke-28"),sQuery(id+"F5.wireOp",EDGE,"E11.sketch_text.stroke-29"),sQuery(id+"F5.wireOp",EDGE,"E11.sketch_text.stroke-30"),sQuery(id+"F5.wireOp",EDGE,"E11.sketch_text.stroke-31"),sQuery(id+"F5.wireOp",EDGE,"E11.sketch_text.stroke-32"),sQuery(id+"F5.wireOp",EDGE,"E11.sketch_text.stroke-33"),sQuery(id+"F5.wireOp",EDGE,"E11.sketch_text.stroke-34"),sQuery(id+"F5.wireOp",EDGE,"E11.sketch_text.stroke-35"),sQuery(id+"F5.wireOp",EDGE,"E11.sketch_text.stroke-36"),sQuery(id+"F5.wireOp",EDGE,"E11.sketch_text.stroke-37"),sQuery(id+"F5.wireOp",EDGE,"E11.sketch_text.stroke-38"),sQuery(id+"F5.wireOp",EDGE,"E11.sketch_text.stroke-39"),sQuery(id+"F5.wireOp",EDGE,"E11.sketch_text.stroke-40"),sQuery(id+"F5.wireOp",EDGE,"E11.sketch_text.stroke-41"),sQuery(id+"F5.wireOp",EDGE,"E11.sketch_text.stroke-42"),sQuery(id+"F5.wireOp",EDGE,"E11.sketch_text.stroke-43"),sQuery(id+"F5.wireOp",EDGE,"E11.sketch_text.stroke-44"),sQuery(id+"F5.wireOp",EDGE,"E11.sketch_text.stroke-45"),sQuery(id+"F5.wireOp",EDGE,"E11.sketch_text.stroke-46"),sQuery(id+"F5.wireOp",EDGE,"E11.sketch_text.stroke-47"),sQuery(id+"F5.wireOp",EDGE,"E11.sketch_text.stroke-48")])],"isStart":false})});
            var Q1;
            Q1=makeQuery(id+"F6.boolean.opBoolean","COPY",FACE,{"derivedFrom":makeQuery(id+"F6.opExtrude","CAP_FACE",FACE,{"disambiguationData":[OSD([sQuery(id+"F5.wireOp",EDGE,"E11.sketch_text.stroke-49"),sQuery(id+"F5.wireOp",EDGE,"E11.sketch_text.stroke-50"),sQuery(id+"F5.wireOp",EDGE,"E11.sketch_text.stroke-51"),sQuery(id+"F5.wireOp",EDGE,"E11.sketch_text.stroke-52"),sQuery(id+"F5.wireOp",EDGE,"E11.sketch_text.stroke-53"),sQuery(id+"F5.wireOp",EDGE,"E11.sketch_text.stroke-54"),sQuery(id+"F5.wireOp",EDGE,"E11.sketch_text.stroke-55"),sQuery(id+"F5.wireOp",EDGE,"E11.sketch_text.stroke-56"),sQuery(id+"F5.wireOp",EDGE,"E11.sketch_text.stroke-57"),sQuery(id+"F5.wireOp",EDGE,"E11.sketch_text.stroke-58"),sQuery(id+"F5.wireOp",EDGE,"E11.sketch_text.stroke-59"),sQuery(id+"F5.wireOp",EDGE,"E11.sketch_text.stroke-60"),sQuery(id+"F5.wireOp",EDGE,"E11.sketch_text.stroke-61"),sQuery(id+"F5.wireOp",EDGE,"E11.sketch_text.stroke-62"),sQuery(id+"F5.wireOp",EDGE,"E11.sketch_text.stroke-63"),sQuery(id+"F5.wireOp",EDGE,"E11.sketch_text.stroke-64"),sQuery(id+"F5.wireOp",EDGE,"E11.sketch_text.stroke-65"),sQuery(id+"F5.wireOp",EDGE,"E11.sketch_text.stroke-66"),sQuery(id+"F5.wireOp",EDGE,"E11.sketch_text.stroke-67"),sQuery(id+"F5.wireOp",EDGE,"E11.sketch_text.stroke-68"),sQuery(id+"F5.wireOp",EDGE,"E11.sketch_text.stroke-69"),sQuery(id+"F5.wireOp",EDGE,"E11.sketch_text.stroke-70"),sQuery(id+"F5.wireOp",EDGE,"E11.sketch_text.stroke-71"),sQuery(id+"F5.wireOp",EDGE,"E11.sketch_text.stroke-72"),sQuery(id+"F5.wireOp",EDGE,"E11.sketch_text.stroke-73"),sQuery(id+"F5.wireOp",EDGE,"E11.sketch_text.stroke-74"),sQuery(id+"F5.wireOp",EDGE,"E11.sketch_text.stroke-75"),sQuery(id+"F5.wireOp",EDGE,"E11.sketch_text.stroke-76"),sQuery(id+"F5.wireOp",EDGE,"E11.sketch_text.stroke-77"),sQuery(id+"F5.wireOp",EDGE,"E11.sketch_text.stroke-78"),sQuery(id+"F5.wireOp",EDGE,"E11.sketch_text.stroke-79"),sQuery(id+"F5.wireOp",EDGE,"E11.sketch_text.stroke-80")])],"isStart":false})});
            var Q2;
            Q2=makeQuery(id+"F6.boolean.opBoolean","COPY",FACE,{"derivedFrom":makeQuery(id+"F6.opExtrude","CAP_FACE",FACE,{"disambiguationData":[OSD([sQuery(id+"F5.wireOp",EDGE,"E11.sketch_text.stroke-81"),sQuery(id+"F5.wireOp",EDGE,"E11.sketch_text.stroke-82"),sQuery(id+"F5.wireOp",EDGE,"E11.sketch_text.stroke-83"),sQuery(id+"F5.wireOp",EDGE,"E11.sketch_text.stroke-84"),sQuery(id+"F5.wireOp",EDGE,"E11.sketch_text.stroke-85"),sQuery(id+"F5.wireOp",EDGE,"E11.sketch_text.stroke-86"),sQuery(id+"F5.wireOp",EDGE,"E11.sketch_text.stroke-87"),sQuery(id+"F5.wireOp",EDGE,"E11.sketch_text.stroke-88"),sQuery(id+"F5.wireOp",EDGE,"E11.sketch_text.stroke-89"),sQuery(id+"F5.wireOp",EDGE,"E11.sketch_text.stroke-90"),sQuery(id+"F5.wireOp",EDGE,"E11.sketch_text.stroke-91"),sQuery(id+"F5.wireOp",EDGE,"E11.sketch_text.stroke-92"),sQuery(id+"F5.wireOp",EDGE,"E11.sketch_text.stroke-93"),sQuery(id+"F5.wireOp",EDGE,"E11.sketch_text.stroke-94"),sQuery(id+"F5.wireOp",EDGE,"E11.sketch_text.stroke-95"),sQuery(id+"F5.wireOp",EDGE,"E11.sketch_text.stroke-96"),sQuery(id+"F5.wireOp",EDGE,"E11.sketch_text.stroke-97"),sQuery(id+"F5.wireOp",EDGE,"E11.sketch_text.stroke-98"),sQuery(id+"F5.wireOp",EDGE,"E11.sketch_text.stroke-99"),sQuery(id+"F5.wireOp",EDGE,"E11.sketch_text.stroke-100"),sQuery(id+"F5.wireOp",EDGE,"E11.sketch_text.stroke-101"),sQuery(id+"F5.wireOp",EDGE,"E11.sketch_text.stroke-102"),sQuery(id+"F5.wireOp",EDGE,"E11.sketch_text.stroke-103"),sQuery(id+"F5.wireOp",EDGE,"E11.sketch_text.stroke-104"),sQuery(id+"F5.wireOp",EDGE,"E11.sketch_text.stroke-105"),sQuery(id+"F5.wireOp",EDGE,"E11.sketch_text.stroke-106"),sQuery(id+"F5.wireOp",EDGE,"E11.sketch_text.stroke-107"),sQuery(id+"F5.wireOp",EDGE,"E11.sketch_text.stroke-108"),sQuery(id+"F5.wireOp",EDGE,"E11.sketch_text.stroke-109"),sQuery(id+"F5.wireOp",EDGE,"E11.sketch_text.stroke-110"),sQuery(id+"F5.wireOp",EDGE,"E11.sketch_text.stroke-111"),sQuery(id+"F5.wireOp",EDGE,"E11.sketch_text.stroke-112"),sQuery(id+"F5.wireOp",EDGE,"E11.sketch_text.stroke-113"),sQuery(id+"F5.wireOp",EDGE,"E11.sketch_text.stroke-114"),sQuery(id+"F5.wireOp",EDGE,"E11.sketch_text.stroke-115"),sQuery(id+"F5.wireOp",EDGE,"E11.sketch_text.stroke-116"),sQuery(id+"F5.wireOp",EDGE,"E11.sketch_text.stroke-117"),sQuery(id+"F5.wireOp",EDGE,"E11.sketch_text.stroke-118"),sQuery(id+"F5.wireOp",EDGE,"E11.sketch_text.stroke-119"),sQuery(id+"F5.wireOp",EDGE,"E11.sketch_text.stroke-120"),sQuery(id+"F5.wireOp",EDGE,"E11.sketch_text.stroke-121"),sQuery(id+"F5.wireOp",EDGE,"E11.sketch_text.stroke-122"),sQuery(id+"F5.wireOp",EDGE,"E11.sketch_text.stroke-123"),sQuery(id+"F5.wireOp",EDGE,"E11.sketch_text.stroke-124"),sQuery(id+"F5.wireOp",EDGE,"E11.sketch_text.stroke-125"),sQuery(id+"F5.wireOp",EDGE,"E11.sketch_text.stroke-126"),sQuery(id+"F5.wireOp",EDGE,"E11.sketch_text.stroke-127"),sQuery(id+"F5.wireOp",EDGE,"E11.sketch_text.stroke-128"),sQuery(id+"F5.wireOp",EDGE,"E11.sketch_text.stroke-129")])],"isStart":false})});
            fillet(context, id + "F10", {"entities" : qUnion([Q0, Q1, Q2]), "radius" : 0.4 * mm, "tangentPropagation" : true, "allowEdgeOverflow" : false});
        }
    });
